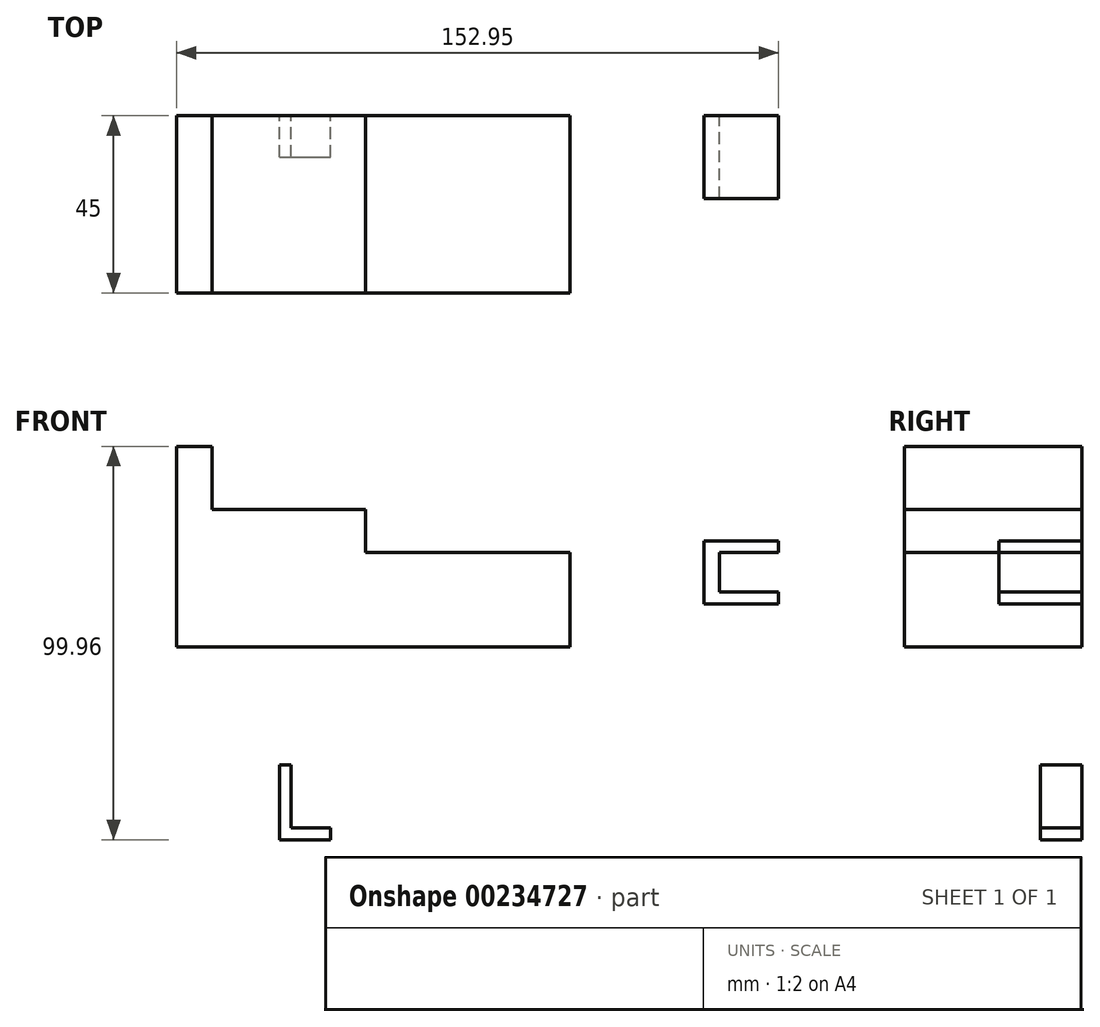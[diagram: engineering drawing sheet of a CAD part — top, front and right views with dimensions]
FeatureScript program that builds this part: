
annotation { "Feature Type Name" : "Feature", "Feature Type Description" : "" }
export const myFeature = defineFeature(function(context is Context, id is Id, definition is map)
    precondition{}
    {
        {
            var Q0;
            Q0=qCreatedBy(makeId("Front.planeOp"),FACE);
            var sketch = newSketch(context, id + "F0", { "sketchPlane" : qUnion([Q0])});
            skLineSegment(sketch, "E0.bottom", {"start": v(-81.3, 72.49) * mm, "end": v(18.7, 72.49) * mm});
            skLineSegment(sketch, "E0.top", {"start": v(-81.3, 21.49) * mm, "end": v(18.7, 21.49) * mm});
            skLineSegment(sketch, "E0.left", {"start": v(-81.3, 72.49) * mm, "end": v(-81.3, 21.49) * mm});
            skLineSegment(sketch, "E0.right", {"start": v(18.7, 72.49) * mm, "end": v(18.7, 21.49) * mm});
            skLineSegment(sketch, "E1.bottom", {"start": v(-72.3, 72.49) * mm, "end": v(18.7, 72.49) * mm});
            skLineSegment(sketch, "E1.top", {"start": v(-72.3, 56.49) * mm, "end": v(18.7, 56.49) * mm});
            skLineSegment(sketch, "E1.left", {"start": v(-72.3, 72.49) * mm, "end": v(-72.3, 56.49) * mm});
            skLineSegment(sketch, "E1.right", {"start": v(18.7, 72.49) * mm, "end": v(18.7, 56.49) * mm});
            skLineSegment(sketch, "E2.bottom", {"start": v(18.7, 21.49) * mm, "end": v(-33.3, 21.49) * mm});
            skLineSegment(sketch, "E2.top", {"start": v(18.7, 45.49) * mm, "end": v(-33.3, 45.49) * mm});
            skLineSegment(sketch, "E2.left", {"start": v(18.7, 21.49) * mm, "end": v(18.7, 45.49) * mm});
            skLineSegment(sketch, "E2.right", {"start": v(-33.3, 21.49) * mm, "end": v(-33.3, 45.49) * mm});
            skLineSegment(sketch, "E3", {"start": v(-33.3, 45.49) * mm, "end": v(-33.3, 56.49) * mm});
            skSolve(sketch);
        }
        {
            var Q0;
            {var subQ3=sQuery(id+"F0.wireOp",EDGE,"E0.left");Q0=makeQuery(id+"F0.imprint","IMPRINT",FACE,{"disambiguationData":[TD([[makeQuery(id+"F0.imprint","IMPRINT",EDGE,{"derivedFrom":subQ3}),1.0]])]});}
            var Q1;
            {var subQ4=sQuery(id+"F0.wireOp",EDGE,"E2.top");Q1=makeQuery(id+"F0.imprint","IMPRINT",FACE,{"disambiguationData":[TD([[makeQuery(id+"F0.imprint","IMPRINT",EDGE,{"derivedFrom":subQ4}),1.0]])]});}
            extrude(context, id + "F1", {"entities" : qUnion([Q0, Q1]), "depth" : 45 * mm, "offsetDistance" : 25 * mm});
        }
        {
            var Q0;
            Q0=qCreatedBy(makeId("Front.planeOp"),FACE);
            var sketch = newSketch(context, id + "F2", { "sketchPlane" : qUnion([Q0])});
            skLineSegment(sketch, "E4.bottom", {"start": v(52.66, 48.49) * mm, "end": v(71.66, 48.49) * mm});
            skLineSegment(sketch, "E4.top", {"start": v(52.66, 32.49) * mm, "end": v(71.66, 32.49) * mm});
            skLineSegment(sketch, "E4.left", {"start": v(52.66, 48.49) * mm, "end": v(52.66, 32.49) * mm});
            skLineSegment(sketch, "E4.right", {"start": v(71.66, 48.49) * mm, "end": v(71.66, 32.49) * mm});
            skLineSegment(sketch, "E5.bottom", {"start": v(71.66, 45.49) * mm, "end": v(56.66, 45.49) * mm});
            skLineSegment(sketch, "E5.top", {"start": v(71.66, 35.49) * mm, "end": v(56.66, 35.49) * mm});
            skLineSegment(sketch, "E5.left", {"start": v(71.66, 45.49) * mm, "end": v(71.66, 35.49) * mm});
            skLineSegment(sketch, "E5.right", {"start": v(56.66, 45.49) * mm, "end": v(56.66, 35.49) * mm});
            skSolve(sketch);
        }
        {
            var Q0;
            {var subQ3=sQuery(id+"F2.wireOp",EDGE,"E4.bottom");Q0=makeQuery(id+"F2.imprint","IMPRINT",FACE,{"disambiguationData":[TD([[makeQuery(id+"F2.imprint","IMPRINT",EDGE,{"derivedFrom":subQ3}),-1.0]])]});}
            extrude(context, id + "F3", {"entities" : qUnion([Q0]), "depth" : 21 * mm, "offsetDistance" : 25 * mm});
        }
        {
            var Q0;
            Q0=qCreatedBy(makeId("Front.planeOp"),FACE);
            var sketch = newSketch(context, id + "F4", { "sketchPlane" : qUnion([Q0])});
            skLineSegment(sketch, "E6.bottom", {"start": v(-55.18, -8.47) * mm, "end": v(-42.18, -8.47) * mm});
            skLineSegment(sketch, "E6.top", {"start": v(-55.18, -27.47) * mm, "end": v(-42.18, -27.47) * mm});
            skLineSegment(sketch, "E6.left", {"start": v(-55.18, -8.47) * mm, "end": v(-55.18, -27.47) * mm});
            skLineSegment(sketch, "E6.right", {"start": v(-42.18, -8.47) * mm, "end": v(-42.18, -27.47) * mm});
            skLineSegment(sketch, "E7.bottom", {"start": v(-52.18, -8.47) * mm, "end": v(-42.18, -8.47) * mm});
            skLineSegment(sketch, "E7.top", {"start": v(-52.18, -24.47) * mm, "end": v(-42.18, -24.47) * mm});
            skLineSegment(sketch, "E7.left", {"start": v(-52.18, -8.47) * mm, "end": v(-52.18, -24.47) * mm});
            skLineSegment(sketch, "E7.right", {"start": v(-42.18, -8.47) * mm, "end": v(-42.18, -24.47) * mm});
            skLineSegment(sketch, "E8", {"start": v(-52.18, -24.47) * mm, "end": v(-55.18, -24.47) * mm});
            skSolve(sketch);
        }
        {
            var Q0;
            {var subQ1=sQuery(id+"F4.wireOp",EDGE,"E6.top");Q0=makeQuery(id+"F4.imprint","IMPRINT",FACE,{"disambiguationData":[TD([[makeQuery(id+"F4.imprint","IMPRINT",EDGE,{"derivedFrom":subQ1}),1.0]])]});}
            var Q1;
            {var subQ0=sQuery(id+"F4.wireOp",EDGE,"E7.left");Q1=makeQuery(id+"F4.imprint","IMPRINT",FACE,{"disambiguationData":[TD([[makeQuery(id+"F4.imprint","IMPRINT",EDGE,{"derivedFrom":subQ0}),-1.0]])]});}
            extrude(context, id + "F5", {"entities" : qUnion([Q0, Q1]), "depth" : 10.5 * mm, "offsetDistance" : 25 * mm});
        }
    });
